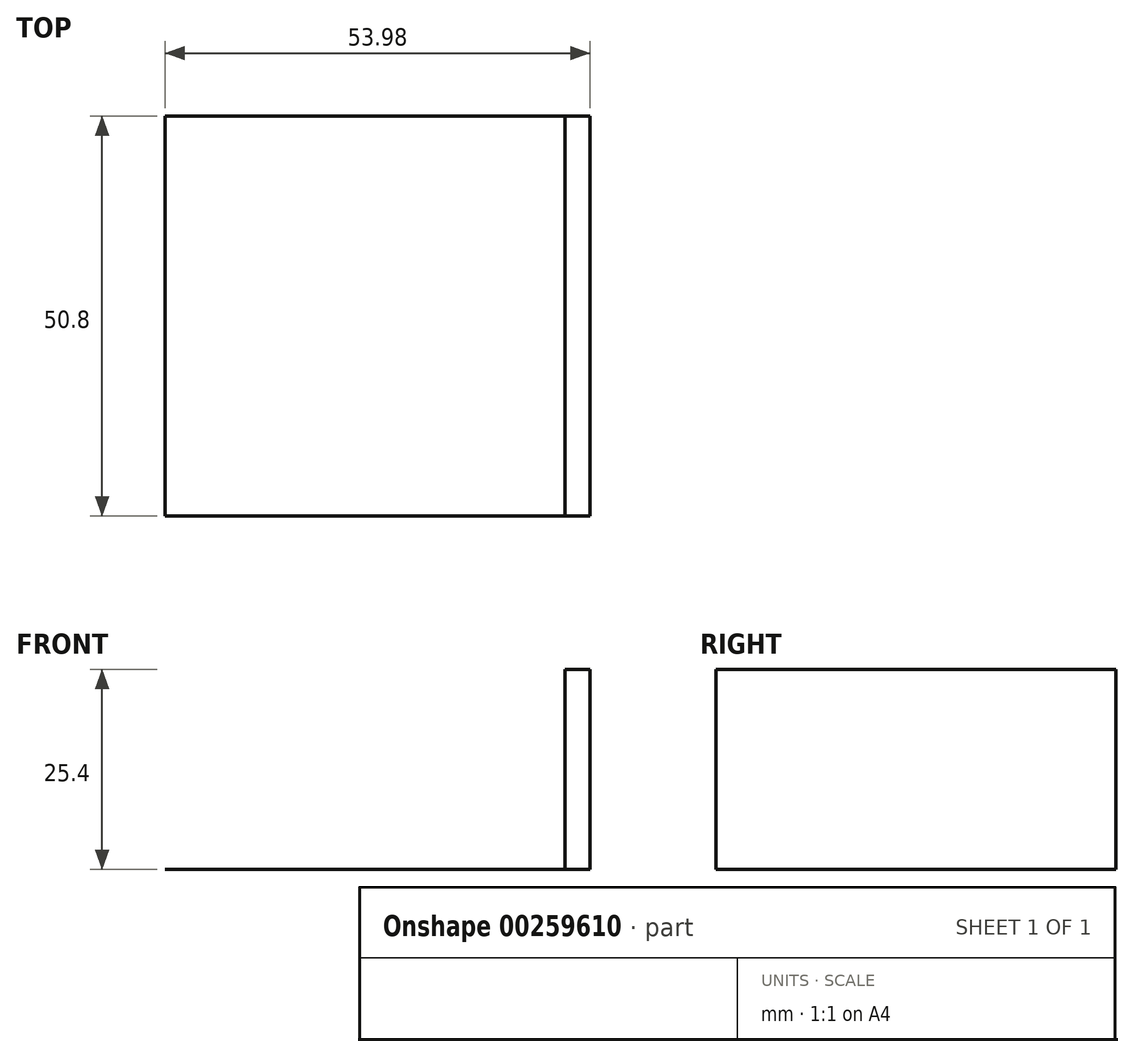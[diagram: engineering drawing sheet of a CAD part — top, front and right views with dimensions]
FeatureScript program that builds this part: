
annotation { "Feature Type Name" : "Feature", "Feature Type Description" : "" }
export const myFeature = defineFeature(function(context is Context, id is Id, definition is map)
    precondition{}
    {
        {
            var Q0;
            Q0=qCreatedBy(makeId("Top.planeOp"),FACE);
            var sketch = newSketch(context, id + "F0", { "sketchPlane" : qUnion([Q0])});
            skLineSegment(sketch, "E0.bottom", {"start": v(0, 0) * mm, "end": v(-53.97, 0) * mm});
            skLineSegment(sketch, "E0.top", {"start": v(0, 50.8) * mm, "end": v(-53.98, 50.8) * mm});
            skLineSegment(sketch, "E0.left", {"start": v(0, 0) * mm, "end": v(0, 50.8) * mm});
            skLineSegment(sketch, "E0.right", {"start": v(-53.97, 0) * mm, "end": v(-53.98, 50.8) * mm});
            skSolve(sketch);
        }
        {
            var Q0;
            Q0=makeQuery(id+"F0.imprint","IMPRINT",FACE,{"disambiguationData":[TD([[makeQuery(id+"F0.imprint","IMPRINT",EDGE,{"derivedFrom":sQuery(id+"F0.wireOp",EDGE,"E0.bottom")}),-1.0]])]});
            extrude(context, id + "F1", {"entities" : qUnion([Q0]), "depth" : 1 / 203.2 * mm});
        }
        {
            var Q0;
            Q0=makeQuery(id+"F1.opExtrude","CAP_FACE",FACE,{"disambiguationData":[OSD([sQuery(id+"F0.wireOp",EDGE,"E0.bottom"),sQuery(id+"F0.wireOp",EDGE,"E0.top"),sQuery(id+"F0.wireOp",EDGE,"E0.left"),sQuery(id+"F0.wireOp",EDGE,"E0.right")])],"isStart":false});
            var sketch = newSketch(context, id + "F2", { "sketchPlane" : qUnion([Q0])});
            skLineSegment(sketch, "E1.bottom", {"start": v(0, 0) * mm, "end": v(-3.18, 0) * mm});
            skLineSegment(sketch, "E1.top", {"start": v(0, 50.8) * mm, "end": v(-3.18, 50.8) * mm});
            skLineSegment(sketch, "E1.left", {"start": v(0, 0) * mm, "end": v(0, 50.8) * mm});
            skLineSegment(sketch, "E1.right", {"start": v(-3.18, 0) * mm, "end": v(-3.18, 50.8) * mm});
            skSolve(sketch);
        }
        {
            var Q0;
            Q0=makeQuery(id+"F2.imprint","IMPRINT",FACE,{"disambiguationData":[TD([[makeQuery(id+"F2.imprint","IMPRINT",EDGE,{"derivedFrom":sQuery(id+"F2.wireOp",EDGE,"E1.bottom")}),-1.0]])]});
            extrude(context, id + "F3", {"entities" : qUnion([Q0]), "operationType" : NewBodyOperationType.ADD, "depth" : 25.4 * mm});
        }
    });
